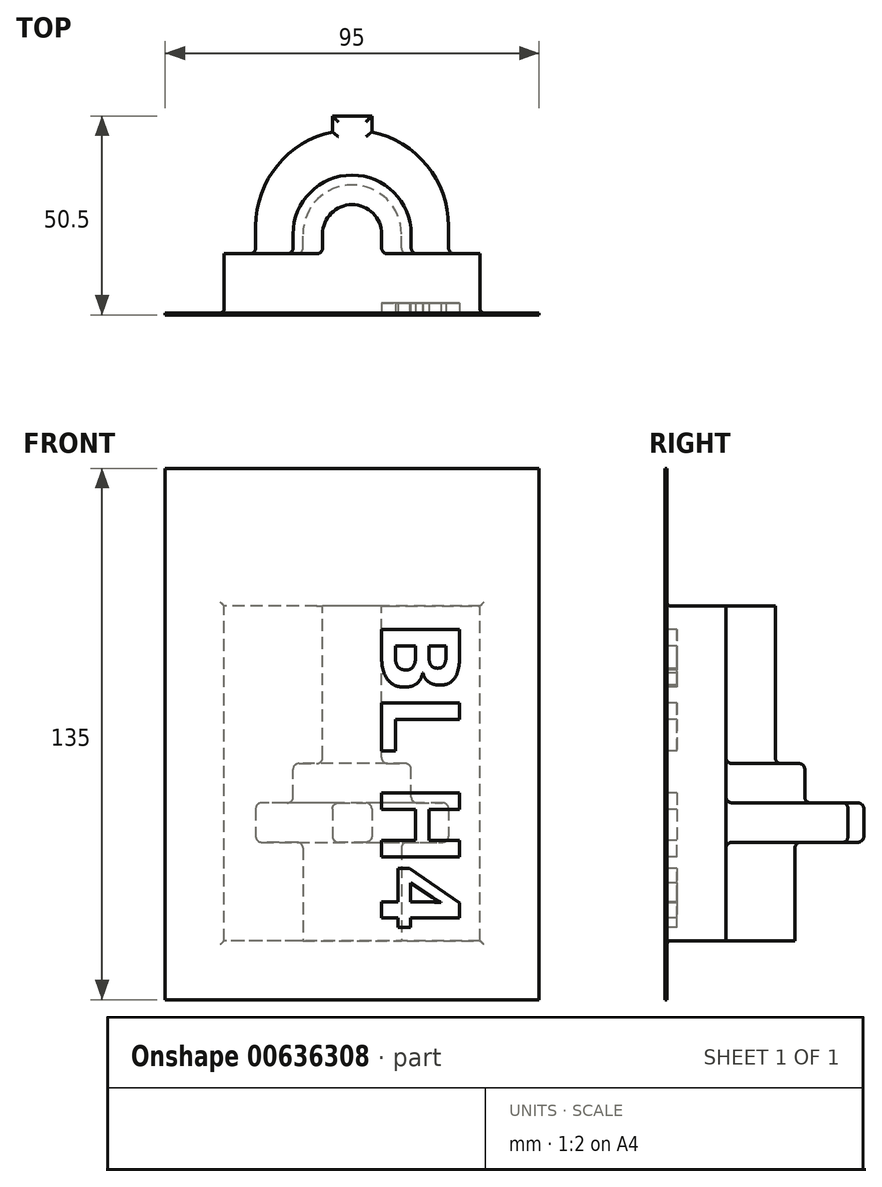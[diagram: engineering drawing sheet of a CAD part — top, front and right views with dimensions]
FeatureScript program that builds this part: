
annotation { "Feature Type Name" : "Feature", "Feature Type Description" : "" }
export const myFeature = defineFeature(function(context is Context, id is Id, definition is map)
    precondition{}
    {
        {
            var Q0;
            Q0=qCreatedBy(makeId("Right.planeOp"),FACE);
            var sketch = newSketch(context, id + "F0", { "sketchPlane" : qUnion([Q0])});
            skLineSegment(sketch, "E0", {"start": v(0, 0) * mm, "end": v(0, 135) * mm});
            skLineSegment(sketch, "E1", {"start": v(0, 135) * mm, "end": v(0.5, 135) * mm});
            skLineSegment(sketch, "E2", {"start": v(0.5, 135) * mm, "end": v(0.5, 100) * mm});
            skLineSegment(sketch, "E3", {"start": v(0.5, 100) * mm, "end": v(50.5, 100) * mm});
            skLineSegment(sketch, "E4", {"start": v(50.5, 100) * mm, "end": v(50.5, 15) * mm});
            skLineSegment(sketch, "E5", {"start": v(50.5, 15) * mm, "end": v(0.5, 15) * mm});
            skLineSegment(sketch, "E6", {"start": v(0.5, 15) * mm, "end": v(0.5, 0) * mm});
            skLineSegment(sketch, "E7", {"start": v(0.5, 0) * mm, "end": v(0, 0) * mm});
            skSolve(sketch);
        }
        {
            var Q0;
            Q0 = qSketchRegion(id + "F0", true);
            extrude(context, id + "F1", {"entities" : qUnion([Q0]), "depth" : 95 * mm, "offsetDistance" : 25 * mm});
        }
        {
            var Q0;
            Q0=makeQuery(id+"F1.opExtrude","SWEPT_FACE",FACE,{"disambiguationData":[OSD([sQuery(id+"F0.wireOp",EDGE,"E4")])]});
            var sketch = newSketch(context, id + "F2", { "sketchPlane" : qUnion([Q0])});
            skLineSegment(sketch, "E8.bottom", {"start": v(-95, 100) * mm, "end": v(-80, 100) * mm});
            skLineSegment(sketch, "E8.top", {"start": v(-95, 15) * mm, "end": v(-80, 15) * mm});
            skLineSegment(sketch, "E8.left", {"start": v(-95, 100) * mm, "end": v(-95, 15) * mm});
            skLineSegment(sketch, "E8.right", {"start": v(-80, 100) * mm, "end": v(-80, 15) * mm});
            skLineSegment(sketch, "E9.bottom", {"start": v(0, 100) * mm, "end": v(-15, 100) * mm});
            skLineSegment(sketch, "E9.top", {"start": v(0, 15) * mm, "end": v(-15, 15) * mm});
            skLineSegment(sketch, "E9.left", {"start": v(0, 100) * mm, "end": v(0, 15) * mm});
            skLineSegment(sketch, "E9.right", {"start": v(-15, 100) * mm, "end": v(-15, 15) * mm});
            skSolve(sketch);
        }
        {
            var Q0;
            Q0 = qSketchRegion(id + "F2", true);
            var Q1;
            Q1=makeQuery(id+"F1.opExtrude","SWEPT_FACE",FACE,{"disambiguationData":[OSD([sQuery(id+"F0.wireOp",EDGE,"E2")])]});
            extrude(context, id + "F3", {"entities" : qUnion([Q0]), "operationType" : NewBodyOperationType.REMOVE, "endBound" : BoundingType.UP_TO_SURFACE, "oppositeDirection" : true, "depth" : 25 * mm, "endBoundEntityFace" : qUnion([Q1]), "offsetDistance" : 25 * mm});
        }
        {
            var Q0;
            Q0=makeQuery(id+"F1.opExtrude","SWEPT_FACE",FACE,{"disambiguationData":[OSD([sQuery(id+"F0.wireOp",EDGE,"E0")])]});
            var sketch = newSketch(context, id + "F4", { "sketchPlane" : qUnion([Q0])});
            skText(sketch, "E10", { "text": "BL H4", "fontName": "OpenSans-Bold.ttf"});
            const initialGuessF4  = {"E10": [0.05501, 0.09659, 0, -1, 0.01999]};
            skSetInitialGuess(sketch, initialGuessF4);
            skSolve(sketch);
        }
        {
            var Q0;
            Q0 = qSketchRegion(id + "F4", true);
            extrude(context, id + "F5", {"entities" : qUnion([Q0]), "operationType" : NewBodyOperationType.REMOVE, "oppositeDirection" : true, "depth" : 3 * mm, "offsetDistance" : 25 * mm});
        }
        {
            var Q0;
            Q0=makeQuery(id+"F1.opExtrude","SWEPT_FACE",FACE,{"disambiguationData":[OSD([sQuery(id+"F0.wireOp",EDGE,"E5")])]});
            var sketch = newSketch(context, id + "F6", { "sketchPlane" : qUnion([Q0])});
            skLineSegment(sketch, "E11", {"start": v(80, -15.5) * mm, "end": v(15, -15.5) * mm});
            skLineSegment(sketch, "E12", {"start": v(72, -15.5) * mm, "end": v(72, -22.5) * mm});
            skLineSegment(sketch, "E13", {"start": v(23, -15.5) * mm, "end": v(23, -22.5) * mm});
            skLineSegment(sketch, "E14", {"start": v(72, -22.5) * mm, "end": v(23, -22.5) * mm});
            skArc(sketch, "E15", {"start": v(72, -22.5) * mm, "mid": v(47.5, -47) * mm, "end": v(23, -22.5) * mm});
            skLineSegment(sketch, "E16", {"start": v(47.5, -49.62) * mm, "end": v(47.5, -35.32) * mm, "construction": true});
            skPoint(sketch, "E16.startSnap0", {"position": v(47.5, -47) * mm});
            skLineSegment(sketch, "E17.bottom", {"start": v(52.5, -47) * mm, "end": v(42.5, -47) * mm});
            skLineSegment(sketch, "E17.top", {"start": v(52.5, -50.5) * mm, "end": v(42.5, -50.5) * mm});
            skLineSegment(sketch, "E17.left", {"start": v(52.5, -47) * mm, "end": v(52.5, -50.5) * mm});
            skLineSegment(sketch, "E17.right", {"start": v(42.5, -47) * mm, "end": v(42.5, -50.5) * mm});
            skLineSegment(sketch, "E18", {"start": v(52.5, -47) * mm, "end": v(52.5, -46.48) * mm});
            skLineSegment(sketch, "E19", {"start": v(42.5, -47) * mm, "end": v(42.5, -46.48) * mm});
            skLineSegment(sketch, "E20", {"start": v(80, -15.5) * mm, "end": v(82.7, -15.5) * mm});
            skLineSegment(sketch, "E21", {"start": v(82.7, -15.5) * mm, "end": v(82.7, -54.56) * mm});
            skLineSegment(sketch, "E22", {"start": v(82.7, -54.56) * mm, "end": v(10.04, -54.56) * mm});
            skLineSegment(sketch, "E23", {"start": v(10.04, -54.56) * mm, "end": v(10.04, -15.5) * mm});
            skLineSegment(sketch, "E24", {"start": v(10.04, -15.5) * mm, "end": v(15, -15.5) * mm});
            skSolve(sketch);
        }
        {
            var Q0;
            {var subQ2=sQuery(id+"F6.wireOp",EDGE,"E13");Q0=makeQuery(id+"F6.imprint","IMPRINT",FACE,{"disambiguationData":[TD([[makeQuery(id+"F6.imprint","IMPRINT",EDGE,{"derivedFrom":subQ2}),-1.0]])]});}
            var Q1;
            {var subQ6=sQuery(id+"F6.wireOp",EDGE,"E17.top");Q1=makeQuery(id+"F6.imprint","IMPRINT",FACE,{"disambiguationData":[TD([[makeQuery(id+"F6.imprint","IMPRINT",EDGE,{"derivedFrom":subQ6}),1.0]])]});}
            var Q2;
            {var subQ1=sQuery(id+"F6.wireOp",EDGE,"E12");Q2=makeQuery(id+"F6.imprint","IMPRINT",FACE,{"disambiguationData":[TD([[makeQuery(id+"F6.imprint","IMPRINT",EDGE,{"derivedFrom":subQ1}),1.0]])]});}
            var Q3;
            Q3=makeQuery(id+"F1.opExtrude","SWEPT_FACE",FACE,{"disambiguationData":[OSD([sQuery(id+"F0.wireOp",EDGE,"E3")])]});
            extrude(context, id + "F7", {"entities" : qUnion([Q0, Q1, Q2]), "operationType" : NewBodyOperationType.REMOVE, "endBound" : BoundingType.UP_TO_SURFACE, "oppositeDirection" : true, "depth" : 25 * mm, "endBoundEntityFace" : qUnion([Q3]), "offsetDistance" : 25 * mm});
        }
        {
            var Q0;
            Q0=makeQuery(id+"F1.opExtrude","SWEPT_FACE",FACE,{"disambiguationData":[OSD([sQuery(id+"F0.wireOp",EDGE,"E5")])]});
            var sketch = newSketch(context, id + "F8", { "sketchPlane" : qUnion([Q0])});
            skLineSegment(sketch, "E25", {"start": v(72, -15.5) * mm, "end": v(23, -15.5) * mm});
            skLineSegment(sketch, "E26", {"start": v(60, -15.5) * mm, "end": v(60, -20.5) * mm});
            skLineSegment(sketch, "E27", {"start": v(35, -15.5) * mm, "end": v(35, -20.5) * mm});
            skLineSegment(sketch, "E28", {"start": v(47.5, -11.9) * mm, "end": v(47.5, -27.14) * mm, "construction": true});
            skPoint(sketch, "E28.startSnap0", {"position": v(47.5, -15.5) * mm});
            skArc(sketch, "E29", {"start": v(60, -20.5) * mm, "mid": v(47.5, -33) * mm, "end": v(35, -20.5) * mm});
            skLineSegment(sketch, "E30", {"start": v(72, -15.5) * mm, "end": v(74.62, -15.5) * mm});
            skLineSegment(sketch, "E31", {"start": v(74.62, -15.5) * mm, "end": v(74.62, -56.44) * mm});
            skLineSegment(sketch, "E32", {"start": v(74.62, -56.44) * mm, "end": v(19.03, -56.44) * mm});
            skLineSegment(sketch, "E33", {"start": v(19.03, -56.44) * mm, "end": v(19.03, -15.5) * mm});
            skLineSegment(sketch, "E34", {"start": v(19.03, -15.5) * mm, "end": v(23, -15.5) * mm});
            skSolve(sketch);
        }
        {
            var Q0;
            Q0=makeQuery(id+"F8.imprint","IMPRINT",FACE,{"disambiguationData":[TD([[makeQuery(id+"F8.imprint","IMPRINT",EDGE,{"derivedFrom":sQuery(id+"F8.wireOp",EDGE,"E30")}),-1.0]])]});
            var Q1;
            {var subQ2=sQuery(id+"F8.wireOp",EDGE,"E33");Q1=makeQuery(id+"F8.imprint","IMPRINT",FACE,{"disambiguationData":[TD([[makeQuery(id+"F8.imprint","IMPRINT",EDGE,{"derivedFrom":subQ2}),-1.0]])]});}
            var Q2;
            {var subQ8=sQuery(id+"F8.wireOp",EDGE,"E26");Q2=makeQuery(id+"F8.imprint","IMPRINT",FACE,{"disambiguationData":[TD([[makeQuery(id+"F8.imprint","IMPRINT",EDGE,{"derivedFrom":subQ8}),1.0]])]});}
            extrude(context, id + "F9", {"entities" : qUnion([Q0, Q1, Q2]), "operationType" : NewBodyOperationType.REMOVE, "oppositeDirection" : true, "depth" : 25 * mm, "offsetDistance" : 25 * mm});
        }
        {
            var Q0;
            Q0=makeQuery(id+"F1.opExtrude","SWEPT_FACE",FACE,{"disambiguationData":[OSD([sQuery(id+"F0.wireOp",EDGE,"E3")])]});
            var sketch = newSketch(context, id + "F10", { "sketchPlane" : qUnion([Q0])});
            skLineSegment(sketch, "E35", {"start": v(23, 15.5) * mm, "end": v(40, 15.5) * mm});
            skLineSegment(sketch, "E36", {"start": v(32.5, 15.5) * mm, "end": v(32.5, 20.5) * mm});
            skLineSegment(sketch, "E37", {"start": v(62.5, 15.5) * mm, "end": v(62.5, 20.5) * mm});
            skLineSegment(sketch, "E38", {"start": v(47.5, 27.59) * mm, "end": v(47.5, 12.21) * mm, "construction": true});
            skPoint(sketch, "E38.startSnap0", {"position": v(47.5, 15.5) * mm});
            skArc(sketch, "E39", {"start": v(32.5, 20.5) * mm, "mid": v(47.5, 35.5) * mm, "end": v(62.5, 20.5) * mm});
            skLineSegment(sketch, "E40.0", {"start": v(55, 15.5) * mm, "end": v(55, 20.5) * mm});
            skArc(sketch, "E40.1", {"start": v(40, 20.5) * mm, "mid": v(47.5, 28) * mm, "end": v(55, 20.5) * mm});
            skLineSegment(sketch, "E40.2", {"start": v(40, 15.5) * mm, "end": v(40, 20.5) * mm});
            skLineSegment(sketch, "E41", {"start": v(23, 15.5) * mm, "end": v(19, 15.5) * mm});
            skLineSegment(sketch, "E42", {"start": v(19, 15.5) * mm, "end": v(19, 57.72) * mm});
            skLineSegment(sketch, "E43", {"start": v(19, 57.72) * mm, "end": v(78.17, 57.72) * mm});
            skLineSegment(sketch, "E44", {"start": v(78.17, 57.72) * mm, "end": v(78.17, 15.5) * mm});
            skLineSegment(sketch, "E45", {"start": v(78.17, 15.5) * mm, "end": v(72, 15.5) * mm});
            skLineSegment(sketch, "E46.trimOffspring", {"start": v(55, 15.5) * mm, "end": v(72, 15.5) * mm});
            skSolve(sketch);
        }
        {
            var Q0;
            Q0=makeQuery(id+"F10.imprint","IMPRINT",FACE,{"disambiguationData":[TD([[makeQuery(id+"F10.imprint","IMPRINT",EDGE,{"derivedFrom":sQuery(id+"F10.wireOp",EDGE,"E41")}),-1.0]])]});
            var Q1;
            {var subQ6=sQuery(id+"F10.wireOp",EDGE,"E36");Q1=makeQuery(id+"F10.imprint","IMPRINT",FACE,{"disambiguationData":[TD([[makeQuery(id+"F10.imprint","IMPRINT",EDGE,{"derivedFrom":subQ6}),1.0]])]});}
            extrude(context, id + "F11", {"entities" : qUnion([Q0, Q1]), "operationType" : NewBodyOperationType.REMOVE, "oppositeDirection" : true, "depth" : 50 * mm, "offsetDistance" : 25 * mm});
        }
        {
            var Q0;
            Q0 = qSketchRegion(id + "F10", true);
            extrude(context, id + "F12", {"entities" : qUnion([Q0]), "operationType" : NewBodyOperationType.REMOVE, "oppositeDirection" : true, "depth" : 40 * mm, "offsetDistance" : 25 * mm});
        }
        {
            var Q0;
            Q0=makeQuery(id+"F12.boolean.opBoolean","COPY",EDGE,{"derivedFrom":makeQuery(id+"F12.opExtrude","SWEPT_EDGE",EDGE,{"disambiguationData":[OSD([sQuery(id+"F10.wireOp",EDGE,"E40.0"),sQuery(id+"F10.wireOp",EDGE,"E46.trimOffspring")])]})});
            var Q1;
            Q1=makeQuery(id+"F12.boolean.opBoolean","COPY",EDGE,{"derivedFrom":makeQuery(id+"F12.opExtrude","CAP_EDGE",EDGE,{"disambiguationData":[OSD([sQuery(id+"F10.wireOp",EDGE,"E45"),sQuery(id+"F10.wireOp",EDGE,"E46.trimOffspring")])],"isStart":false})});
            var Q2;
            Q2=makeQuery(id+"F11.boolean.opBoolean","COPY",EDGE,{"derivedFrom":makeQuery(id+"F11.opExtrude","SWEPT_EDGE",EDGE,{"disambiguationData":[OSD([sQuery(id+"F10.wireOp",EDGE,"E37"),sQuery(id+"F10.wireOp",EDGE,"E46.trimOffspring")])]})});
            var Q3;
            Q3=makeQuery(id+"F11.boolean.opBoolean","COPY",EDGE,{"derivedFrom":makeQuery(id+"F11.opExtrude","CAP_EDGE",EDGE,{"disambiguationData":[OSD([sQuery(id+"F10.wireOp",EDGE,"E45"),sQuery(id+"F10.wireOp",EDGE,"E46.trimOffspring")])],"isStart":false})});
            var Q4;
            Q4=makeQuery(id+"F7.boolean.opBoolean","COPY",EDGE,{"derivedFrom":makeQuery(id+"F7.opExtrude","SWEPT_EDGE",EDGE,{"disambiguationData":[OSD([sQuery(id+"F6.wireOp",EDGE,"E11"),sQuery(id+"F6.wireOp",EDGE,"E12")])]})});
            var Q5;
            Q5=makeQuery(id+"F9.boolean.opBoolean","COPY",EDGE,{"derivedFrom":makeQuery(id+"F9.opExtrude","SWEPT_EDGE",EDGE,{"disambiguationData":[OSD([sQuery(id+"F8.wireOp",EDGE,"E25"),sQuery(id+"F8.wireOp",EDGE,"E26")])]})});
            var Q6;
            Q6=makeQuery(id+"F9.boolean.opBoolean","COPY",EDGE,{"derivedFrom":makeQuery(id+"F9.opExtrude","CAP_EDGE",EDGE,{"disambiguationData":[OSD([sQuery(id+"F8.wireOp",EDGE,"E25"),sQuery(id+"F8.wireOp",EDGE,"E30")])],"isStart":false})});
            var Q7;
            Q7=makeQuery(id+"F12.boolean.opBoolean","COPY",EDGE,{"derivedFrom":makeQuery(id+"F12.opExtrude","CAP_EDGE",EDGE,{"disambiguationData":[OSD([sQuery(id+"F10.wireOp",EDGE,"E35"),sQuery(id+"F10.wireOp",EDGE,"E41")])],"isStart":false})});
            var Q8;
            Q8=makeQuery(id+"F11.boolean.opBoolean","COPY",EDGE,{"derivedFrom":makeQuery(id+"F11.opExtrude","CAP_EDGE",EDGE,{"disambiguationData":[OSD([sQuery(id+"F10.wireOp",EDGE,"E35"),sQuery(id+"F10.wireOp",EDGE,"E41")])],"isStart":false})});
            var Q9;
            Q9=makeQuery(id+"F12.boolean.opBoolean","COPY",EDGE,{"derivedFrom":makeQuery(id+"F12.opExtrude","SWEPT_EDGE",EDGE,{"disambiguationData":[OSD([sQuery(id+"F10.wireOp",EDGE,"E35"),sQuery(id+"F10.wireOp",EDGE,"E40.2")])]})});
            var Q10;
            Q10=makeQuery(id+"F11.boolean.opBoolean","COPY",EDGE,{"derivedFrom":makeQuery(id+"F11.opExtrude","SWEPT_EDGE",EDGE,{"disambiguationData":[OSD([sQuery(id+"F10.wireOp",EDGE,"E35"),sQuery(id+"F10.wireOp",EDGE,"E36")])]})});
            var Q11;
            Q11=makeQuery(id+"F7.boolean.opBoolean","COPY",EDGE,{"derivedFrom":makeQuery(id+"F7.opExtrude","SWEPT_EDGE",EDGE,{"disambiguationData":[OSD([sQuery(id+"F6.wireOp",EDGE,"E11"),sQuery(id+"F6.wireOp",EDGE,"E13")])]})});
            var Q12;
            Q12=makeQuery(id+"F9.boolean.opBoolean","COPY",EDGE,{"derivedFrom":makeQuery(id+"F9.opExtrude","SWEPT_EDGE",EDGE,{"disambiguationData":[OSD([sQuery(id+"F8.wireOp",EDGE,"E25"),sQuery(id+"F8.wireOp",EDGE,"E27")])]})});
            var Q13;
            Q13=makeQuery(id+"F9.boolean.opBoolean","COPY",EDGE,{"derivedFrom":makeQuery(id+"F9.opExtrude","CAP_EDGE",EDGE,{"disambiguationData":[OSD([sQuery(id+"F8.wireOp",EDGE,"E25"),sQuery(id+"F8.wireOp",EDGE,"E34")])],"isStart":false})});
            var Q14;
            Q14=makeQuery(id+"F12.boolean.opBoolean","COPY",EDGE,{"derivedFrom":makeQuery(id+"F12.opExtrude","CAP_EDGE",EDGE,{"disambiguationData":[OSD([sQuery(id+"F10.wireOp",EDGE,"E40.2")])],"isStart":false})});
            var Q15;
            Q15=makeQuery(id+"F11.boolean.opBoolean","COPY",EDGE,{"derivedFrom":makeQuery(id+"F11.opExtrude","CAP_EDGE",EDGE,{"disambiguationData":[OSD([sQuery(id+"F10.wireOp",EDGE,"E39")])],"isStart":false})});
            var Q16;
            Q16=makeQuery(id+"F12.boolean.opBoolean","INTERSECT",EDGE,{"derivedFrom":[makeQuery(id+"F11.boolean.opBoolean","COPY",FACE,{"derivedFrom":makeQuery(id+"F11.opExtrude","SWEPT_FACE",FACE,{"disambiguationData":[OSD([sQuery(id+"F10.wireOp",EDGE,"E39")])]})}),makeQuery(id+"F12.opExtrude","CAP_FACE",FACE,{"disambiguationData":[OSD([sQuery(id+"F10.wireOp",EDGE,"E35"),sQuery(id+"F10.wireOp",EDGE,"E40.0"),sQuery(id+"F10.wireOp",EDGE,"E40.1"),sQuery(id+"F10.wireOp",EDGE,"E40.2"),sQuery(id+"F10.wireOp",EDGE,"E41"),sQuery(id+"F10.wireOp",EDGE,"E42"),sQuery(id+"F10.wireOp",EDGE,"E43"),sQuery(id+"F10.wireOp",EDGE,"E44"),sQuery(id+"F10.wireOp",EDGE,"E45"),sQuery(id+"F10.wireOp",EDGE,"E46.trimOffspring")])],"isStart":false})]});
            var Q17;
            {var subQ0=sQuery(id+"F6.wireOp",EDGE,"E15");Q17=makeQuery(id+"F11.boolean.opBoolean","INTERSECT",EDGE,{"derivedFrom":[makeQuery(id+"F7.boolean.opBoolean","COPY",FACE,{"derivedFrom":makeQuery(id+"F7.opExtrude","SWEPT_FACE",FACE,{"disambiguationData":[OSD([subQ0]),TDD([makeQuery(id+"F6.imprint","IMPRINT",EDGE,{"disambiguationData":[TD([[makeQuery(id+"F6.imprint","INTERSECT",VERTEX,{"derivedFrom":[subQ0,sQuery(id+"F6.wireOp",EDGE,"E18")]}),1.0]])],"derivedFrom":subQ0})])]})}),makeQuery(id+"F11.opExtrude","CAP_FACE",FACE,{"disambiguationData":[OSD([sQuery(id+"F10.wireOp",EDGE,"E35"),sQuery(id+"F10.wireOp",EDGE,"E36"),sQuery(id+"F10.wireOp",EDGE,"E37"),sQuery(id+"F10.wireOp",EDGE,"E39"),sQuery(id+"F10.wireOp",EDGE,"E41"),sQuery(id+"F10.wireOp",EDGE,"E42"),sQuery(id+"F10.wireOp",EDGE,"E43"),sQuery(id+"F10.wireOp",EDGE,"E44"),sQuery(id+"F10.wireOp",EDGE,"E45"),sQuery(id+"F10.wireOp",EDGE,"E46.trimOffspring")])],"isStart":false})]});}
            var Q18;
            {var subQ0=sQuery(id+"F6.wireOp",EDGE,"E15");Q18=makeQuery(id+"F11.boolean.opBoolean","INTERSECT",EDGE,{"derivedFrom":[makeQuery(id+"F7.boolean.opBoolean","COPY",FACE,{"derivedFrom":makeQuery(id+"F7.opExtrude","SWEPT_FACE",FACE,{"disambiguationData":[OSD([subQ0]),TDD([makeQuery(id+"F6.imprint","IMPRINT",EDGE,{"disambiguationData":[TD([[makeQuery(id+"F6.imprint","INTERSECT",VERTEX,{"derivedFrom":[subQ0,sQuery(id+"F6.wireOp",EDGE,"E19")]}),-1.0]])],"derivedFrom":subQ0})])]})}),makeQuery(id+"F11.opExtrude","CAP_FACE",FACE,{"disambiguationData":[OSD([sQuery(id+"F10.wireOp",EDGE,"E35"),sQuery(id+"F10.wireOp",EDGE,"E36"),sQuery(id+"F10.wireOp",EDGE,"E37"),sQuery(id+"F10.wireOp",EDGE,"E39"),sQuery(id+"F10.wireOp",EDGE,"E41"),sQuery(id+"F10.wireOp",EDGE,"E42"),sQuery(id+"F10.wireOp",EDGE,"E43"),sQuery(id+"F10.wireOp",EDGE,"E44"),sQuery(id+"F10.wireOp",EDGE,"E45"),sQuery(id+"F10.wireOp",EDGE,"E46.trimOffspring")])],"isStart":false})]});}
            var Q19;
            Q19=makeQuery(id+"F11.boolean.opBoolean","COPY",FACE,{"derivedFrom":makeQuery(id+"F11.opExtrude","CAP_FACE",FACE,{"disambiguationData":[OSD([sQuery(id+"F10.wireOp",EDGE,"E35"),sQuery(id+"F10.wireOp",EDGE,"E36"),sQuery(id+"F10.wireOp",EDGE,"E37"),sQuery(id+"F10.wireOp",EDGE,"E39"),sQuery(id+"F10.wireOp",EDGE,"E41"),sQuery(id+"F10.wireOp",EDGE,"E42"),sQuery(id+"F10.wireOp",EDGE,"E43"),sQuery(id+"F10.wireOp",EDGE,"E44"),sQuery(id+"F10.wireOp",EDGE,"E45"),sQuery(id+"F10.wireOp",EDGE,"E46.trimOffspring")])],"isStart":false})});
            var Q20;
            Q20=makeQuery(id+"F9.boolean.opBoolean","COPY",FACE,{"derivedFrom":makeQuery(id+"F9.opExtrude","CAP_FACE",FACE,{"disambiguationData":[OSD([sQuery(id+"F8.wireOp",EDGE,"E25"),sQuery(id+"F8.wireOp",EDGE,"E26"),sQuery(id+"F8.wireOp",EDGE,"E27"),sQuery(id+"F8.wireOp",EDGE,"E29"),sQuery(id+"F8.wireOp",EDGE,"E30"),sQuery(id+"F8.wireOp",EDGE,"E31"),sQuery(id+"F8.wireOp",EDGE,"E32"),sQuery(id+"F8.wireOp",EDGE,"E33"),sQuery(id+"F8.wireOp",EDGE,"E34")])],"isStart":false})});
            fillet(context, id + "F13", {"entities" : qUnion([Q0, Q1, Q2, Q3, Q4, Q5, Q6, Q7, Q8, Q9, Q10, Q11, Q12, Q13, Q14, Q15, Q16, Q17, Q18, Q19, Q20]), "radius" : 1.5 * mm, "tangentPropagation" : true, "allowEdgeOverflow" : false});
        }
        {
            var Q0;
            Q0=makeQuery(id+"F3.boolean.opBoolean","COPY",EDGE,{"derivedFrom":makeQuery(id+"F3.opExtrude","CAP_EDGE",EDGE,{"disambiguationData":[OSD([sQuery(id+"F2.wireOp",EDGE,"E8.right")])],"isStart":false})});
            var Q1;
            Q1=makeQuery(id+"F1.opExtrude","SWEPT_EDGE",EDGE,{"disambiguationData":[OSD([sQuery(id+"F0.wireOp",EDGE,"E5"),sQuery(id+"F0.wireOp",EDGE,"E6")])]});
            var Q2;
            Q2=makeQuery(id+"F1.opExtrude","SWEPT_EDGE",EDGE,{"disambiguationData":[OSD([sQuery(id+"F0.wireOp",EDGE,"E2"),sQuery(id+"F0.wireOp",EDGE,"E3")])]});
            var Q3;
            Q3=makeQuery(id+"F3.boolean.opBoolean","COPY",EDGE,{"derivedFrom":makeQuery(id+"F3.opExtrude","CAP_EDGE",EDGE,{"disambiguationData":[OSD([sQuery(id+"F2.wireOp",EDGE,"E9.right")])],"isStart":false})});
            fillet(context, id + "F14", {"entities" : qUnion([Q0, Q1, Q2, Q3]), "radius" : 1 * mm, "tangentPropagation" : true, "allowEdgeOverflow" : false});
        }
    });
